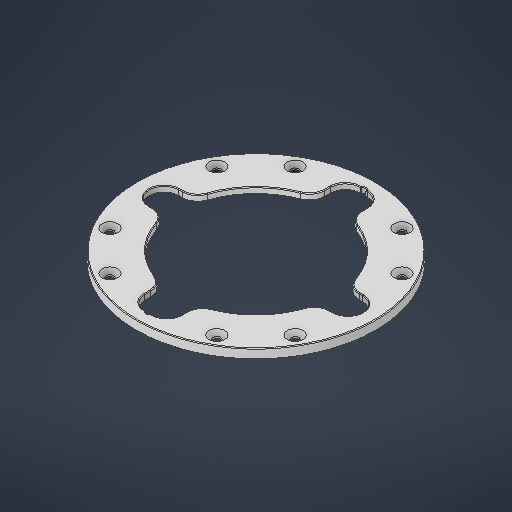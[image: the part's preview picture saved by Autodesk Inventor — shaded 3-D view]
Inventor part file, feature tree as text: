
AUTODESK INVENTOR PART (.ipt)
format: ipt  version: 2025 (Build 290162000, 162)  size: 351,232 bytes
history: native  units: in
note: dims shown in document units (in); Inventor stores cm internally (conversion verified against a paired STEP export)
features: sketch x3, extrude x3, hole x2, chamfer x1
ambient origin geometry x8: Origin, YZ Plane, XZ Plane, XY Plane, X Axis, Y Axis, Z Axis, Center Point
bodies: Solid1 (feature_tree)
feature tree (9):
  sketch  "Sketch1"  dims[d0=6.6929in d1=6.3386in]
  extrude  "Extrusion1"  Depth=6.3386in
  extrude  "Extrusion2"  Depth=5.9843in
  sketch  "Sketch2"  dims[d4=0.8268in d5=1.0236in d6=6.0236in d7=0.4134in d8=0.4134in d9=0.4331in d10=0.2559in d11=0.0in d12=0.1575in d13=0.0in d14=5.9843in d15=0.0787in d16=0.0787in d17=0.2165in d18=4.7244in d20=360.0deg d22=0.1575in d23=0.0in d27=0.1378in d28=0.2362in d29=0.1575in d30=0.0787in d31=90.0deg d32=0.3465in d33=0.0in d34=0.0197in d35=0.0787in d36=45.0deg d37=0.1628in d38=0.3937in d39=0.4409in d40=0.0787in d41=90.0deg d42=0.5591in d43=0.0in]
  extrude  "Extrusion3"  Depth=0.3937in
  hole  "Hole1"  [1 undecoded]
  chamfer  "Chamfer2"  Distance=0.4134in
  hole  "Hole2"  [1 undecoded]
  sketch  "Sketch Circular Pattern1"  dims[d2=4.3701in d3=5.9843in]
note: 2 required parameter values undecoded (feature->parameter linkage not recoverable at this tier; creation-order binding heuristic only, values carry confidence <= 0.55)
